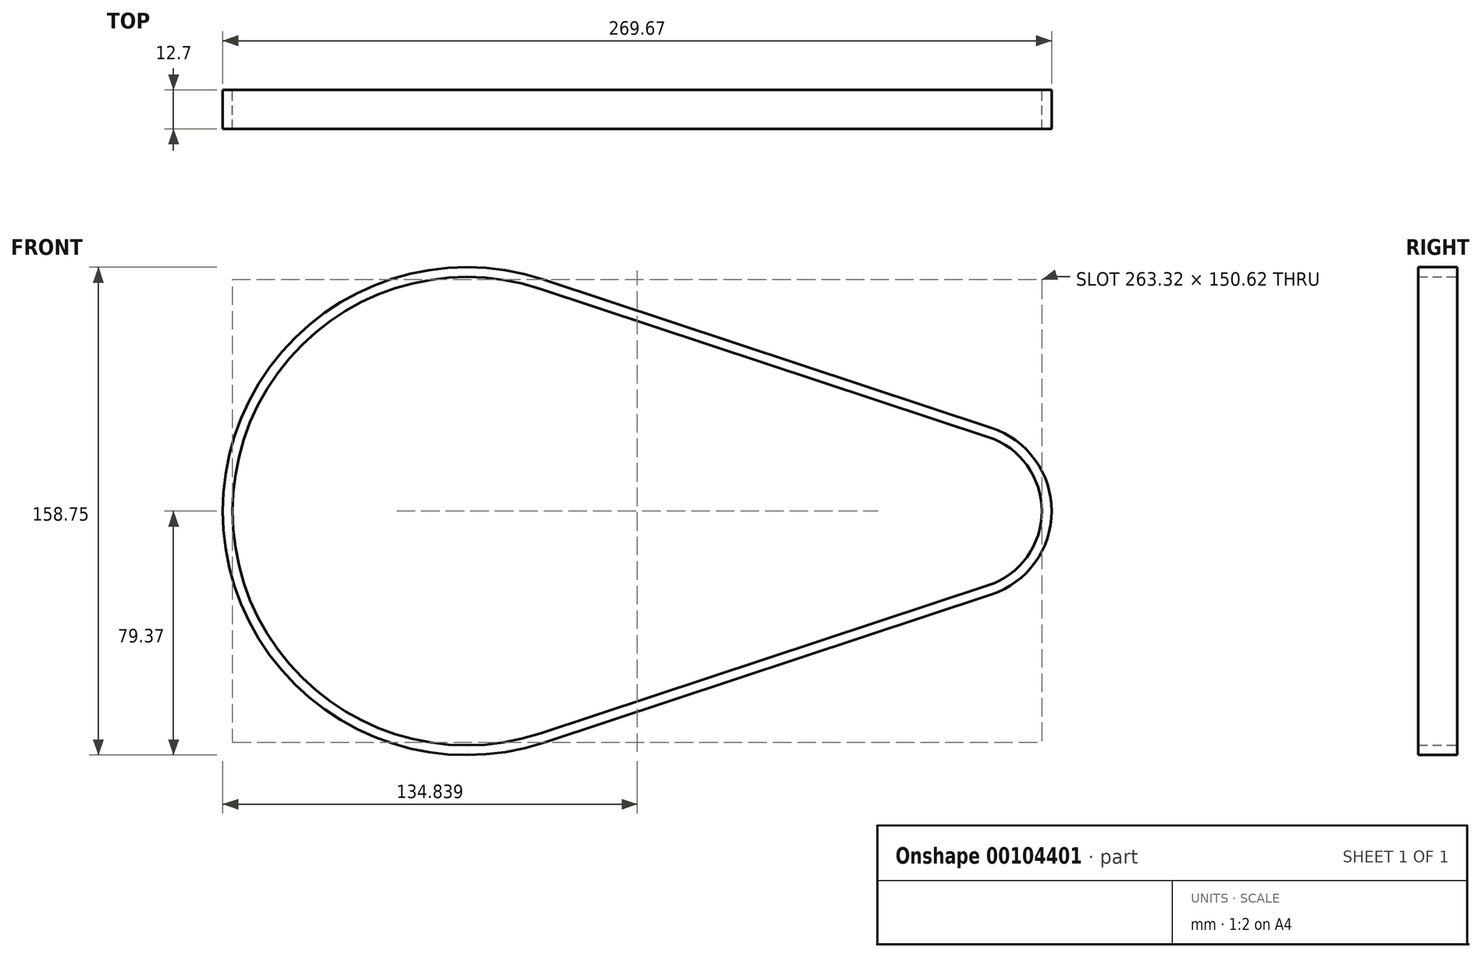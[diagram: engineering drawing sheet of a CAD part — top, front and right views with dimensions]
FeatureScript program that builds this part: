
annotation { "Feature Type Name" : "Feature", "Feature Type Description" : "" }
export const myFeature = defineFeature(function(context is Context, id is Id, definition is map)
    precondition{}
    {
        {
            var Q0;
            Q0=qCreatedBy(makeId("Front.planeOp"),FACE);
            var sketch = newSketch(context, id + "F0", { "sketchPlane" : qUnion([Q0])});
            skCircle(sketch, "E0", {"center": v(0, 0) * mm, "radius": 76.2 * mm});
            skSolve(sketch);
        }
        {
            var Q0;
            Q0=makeQuery(id+"F0.imprint","IMPRINT",FACE,{"disambiguationData":[TD([[makeQuery(id+"F0.imprint","IMPRINT",EDGE,{"derivedFrom":sQuery(id+"F0.wireOp",EDGE,"E0")}),1.0]])]});
            var sketch = newSketch(context, id + "F1", { "sketchPlane" : qUnion([Q0])});
            skArc(sketch, "E1", {"start": v(23.94, 72.34) * mm, "mid": v(-76.2, 0) * mm, "end": v(23.94, -72.34) * mm});
            skArc(sketch, "E2", {"start": v(169.7, -24.11) * mm, "mid": v(187.12, 0) * mm, "end": v(169.7, 24.11) * mm});
            skLineSegment(sketch, "E3", {"start": v(23.94, 72.34) * mm, "end": v(169.7, 24.11) * mm});
            skLineSegment(sketch, "E4", {"start": v(23.94, -72.34) * mm, "end": v(169.7, -24.11) * mm});
            skLineSegment(sketch, "E5.0", {"start": v(24.93, 75.36) * mm, "end": v(170.7, 27.13) * mm});
            skArc(sketch, "E6.0", {"start": v(24.93, 75.36) * mm, "mid": v(-79.38, 0) * mm, "end": v(24.93, -75.36) * mm});
            skLineSegment(sketch, "E7.0", {"start": v(24.93, -75.36) * mm, "end": v(170.7, -27.13) * mm});
            skArc(sketch, "E8.0", {"start": v(170.7, -27.13) * mm, "mid": v(190.3, 0) * mm, "end": v(170.7, 27.13) * mm});
            skSolve(sketch);
        }
        {
            var Q0;
            Q0 = qSketchRegion(id + "F1", true);
            extrude(context, id + "F2", {"entities" : qUnion([Q0]), "depth" : 12.7 * mm});
        }
    });
